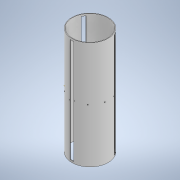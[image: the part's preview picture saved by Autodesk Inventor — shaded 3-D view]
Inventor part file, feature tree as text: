
AUTODESK INVENTOR PART (.ipt)
format: ipt  version: 2021 (Build 250183000, 183)  size: 258,048 bytes
history: native  units: in
note: dims shown in document units (in); Inventor stores cm internally (conversion verified against a paired STEP export)
features: other x28, hole x7, pattern_circular x6, sketch x6, plane x5, extrude x2
ambient origin geometry x8: Origin, YZ Plane, XZ Plane, XY Plane, X Axis, Y Axis, Z Axis, Center Point
bodies: Solid1 (feature_tree)
feature tree (54):
  extrude  "Extrusion1"  Depth=0.3937in
  plane  "Work Plane1"
  extrude  "Extrusion2"  Depth=0.3937in TaperAngle=0.0deg
  pattern_circular  "Circular Pattern1"  Count=3 Angle=360.0deg
  other  "Work Axis1"
  other  "Work Axis2"
  other  "Work Axis3"
  other  "Work Axis4"
  other  "Work Point1"
  other  "Work Point2"
  other  "Work Point3"
  other  "Central Plane"
  other  "Work Point4"
  other  "Work Axis6"
  other  "Work Axis7"
  other  "Offset Plane A"
  other  "Work Point5"
  other  "Work Point6"
  other  "Work Axis8"
  other  "Work Axis9"
  other  "Work Point7"
  other  "Work Point8"
  plane  "Work Plane5"
  plane  "Work Plane6"
  hole  "Hole1"  [1 undecoded]
  hole  "Hole2"  [1 undecoded]
  pattern_circular  "Circular Pattern3"  Count=3 Angle=360.0deg
  sketch  "Sketch5"  dims[d13=0.0484in d14=-11.811in]
  plane  "Work Plane7"
  sketch  "Sketch6"  dims[d15=0.0484in d16=0.1574in]
  hole  "Hole3"  [1 undecoded]
  other  "Work Axis10"
  hole  "Hole4"  [1 undecoded]
  pattern_circular  "Circular Pattern5"  Count=4 Angle=360.0deg
  plane  "Work Plane12"
  hole  "Hole5"  [1 undecoded]
  pattern_circular  "Circular Pattern6"  Count=3 Angle=360.0deg
  other  "plane for insert hole 1"
  sketch  "Sketch7"  dims[d17=-0.1574in]
  other  "plane for insert hole 2"
  hole  "insert hole 2"  [1 undecoded]
  hole  "insert hole 1"  [1 undecoded]
  pattern_circular  "Circular Pattern7"  [2 undecoded]
  pattern_circular  "Circular Pattern9"  [2 undecoded]
  sketch  "Sketch1"  dims[d3=0.0in d5=0.3937in]
  sketch  "Sketch2"  dims[d7=0.3937in d8=0.5in d9=0.0in d10=1.1811in d11=360.0deg]
  other  "Work Axis5"
  other  "Offset Plane B"
  other  "Work Axis11"
  other  "Work Axis12"
  other  "Work Point9"
  other  "Work Axis13"
  other  "Work Point10"
  sketch  "Sketch8"  dims[d48=1.0in d49=1.0in d29=0.096in d30=0.75in d31=0.185in d32=0.25in d33=0.5635in d34=1.0in d35=0.0in d52=1.0in d53=1.0in d38=0.096in d39=0.75in d40=0.185in d41=0.25in d42=0.5635in d43=1.0in d44=0.8108in d45=1.1811in d46=360.0deg d51=0.38in d54=0.177in d55=0.328in d56=0.332in d57=0.25in d58=0.5635in d59=0.484in d60=0.8108in d64=0.19in d65=0.177in d66=0.3229in d67=0.332in d68=0.25in d69=0.5635in d70=0.484in d71=0.8108in d72=1.5748in d73=360.0deg d75=60.0deg d76=1.0in d77=1.0in d78=0.129in d79=0.3229in d80=0.225in d81=0.25in d82=0.5635in d83=0.484in d84=0.8108in d85=1.1811in d86=360.0deg d88=0.2749in d89=0.2749in d90=0.0in d91=0.0in d92=0.0in d93=11.811in d94=0.0in d95=11.811in d96=0.129in d97=0.224in d98=0.225in d99=0.25in d100=0.5635in d101=0.349in d102=0.8108in d103=0.129in d104=0.224in d105=0.225in d106=0.25in d107=0.5635in d108=0.349in d109=0.8108in d110=1.1811in d111=360.0deg d116=1.1811in d117=360.0deg d61=0.75in d62=0.8108in d63=0.0625in]
note: 11 required parameter values undecoded (feature->parameter linkage not recoverable at this tier; creation-order binding heuristic only, values carry confidence <= 0.55)
